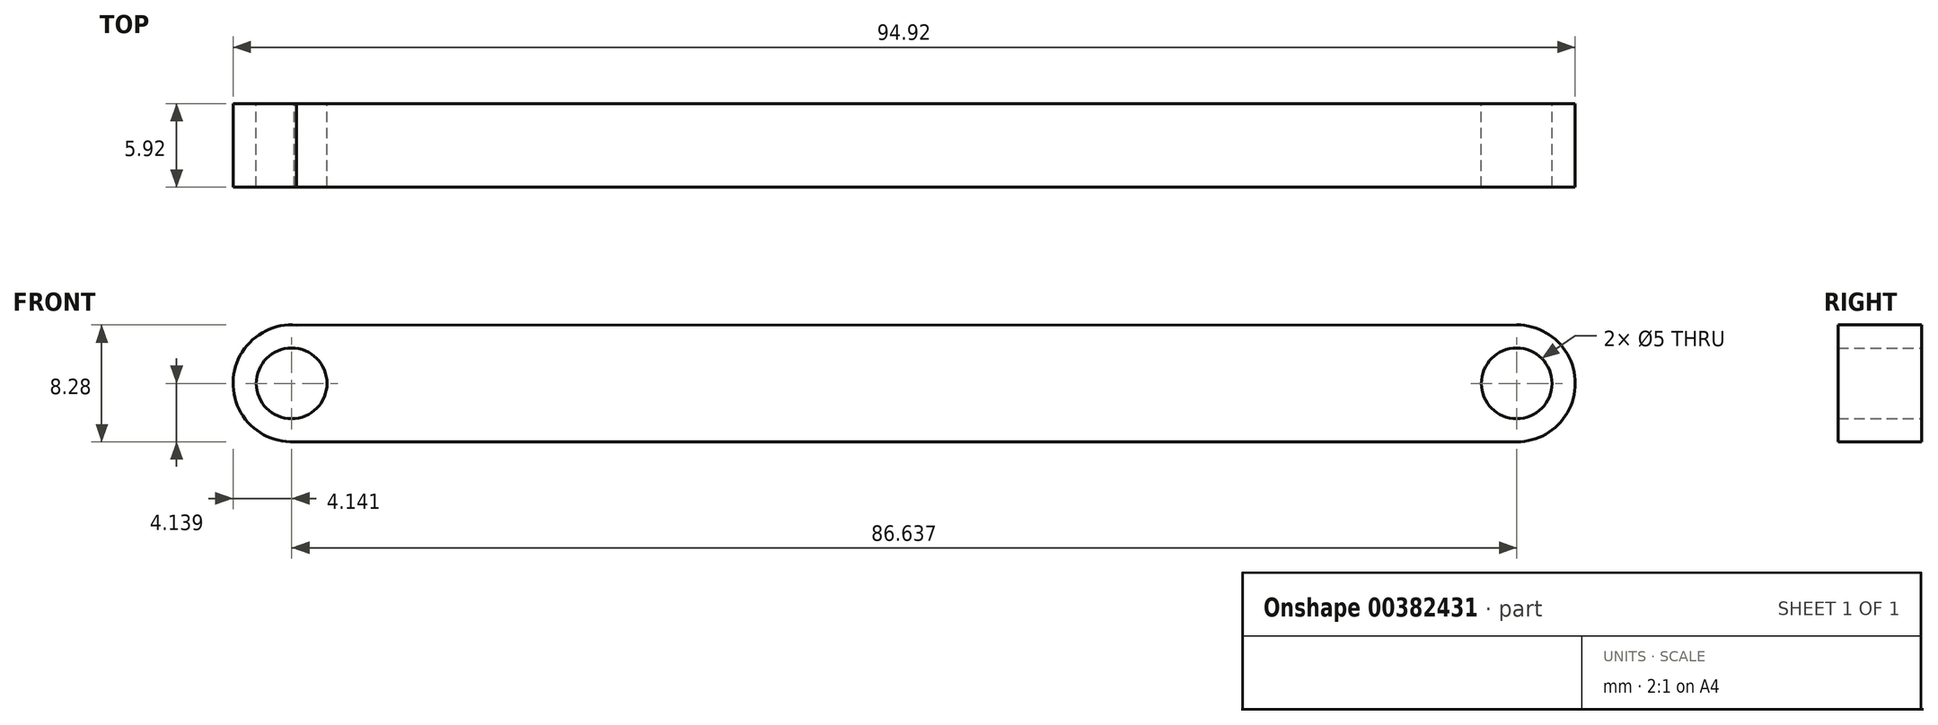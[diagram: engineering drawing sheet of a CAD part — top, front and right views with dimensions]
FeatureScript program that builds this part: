
annotation { "Feature Type Name" : "Feature", "Feature Type Description" : "" }
export const myFeature = defineFeature(function(context is Context, id is Id, definition is map)
    precondition{}
    {
        {
            var Q0;
            Q0=qCreatedBy(makeId("Front.planeOp"),FACE);
            var sketch = newSketch(context, id + "F0", { "sketchPlane" : qUnion([Q0])});
            skArc(sketch, "E0", {"start": v(-53.61, 24.89) * mm, "mid": v(-58.1, 20.85) * mm, "end": v(-53.79, 16.62) * mm});
            skArc(sketch, "E1", {"start": v(32.68, 16.62) * mm, "mid": v(36.82, 20.76) * mm, "end": v(32.68, 24.9) * mm});
            skLineSegment(sketch, "E2", {"start": v(-53.61, 24.89) * mm, "end": v(32.68, 24.9) * mm});
            skLineSegment(sketch, "E3", {"start": v(-53.79, 16.62) * mm, "end": v(32.68, 16.62) * mm});
            skCircle(sketch, "E4", {"center": v(-53.96, 20.76) * mm, "radius": 2.5 * mm});
            skCircle(sketch, "E5", {"center": v(32.68, 20.76) * mm, "radius": 2.5 * mm});
            skSolve(sketch);
        }
        {
            var Q0;
            Q0=makeQuery(id+"F0.imprint","IMPRINT",FACE,{"disambiguationData":[TD([[makeQuery(id+"F0.imprint","IMPRINT",EDGE,{"derivedFrom":sQuery(id+"F0.wireOp",EDGE,"E0")}),1.0]])]});
            extrude(context, id + "F1", {"entities" : qUnion([Q0]), "depth" : 5.92 * mm});
        }
    });
